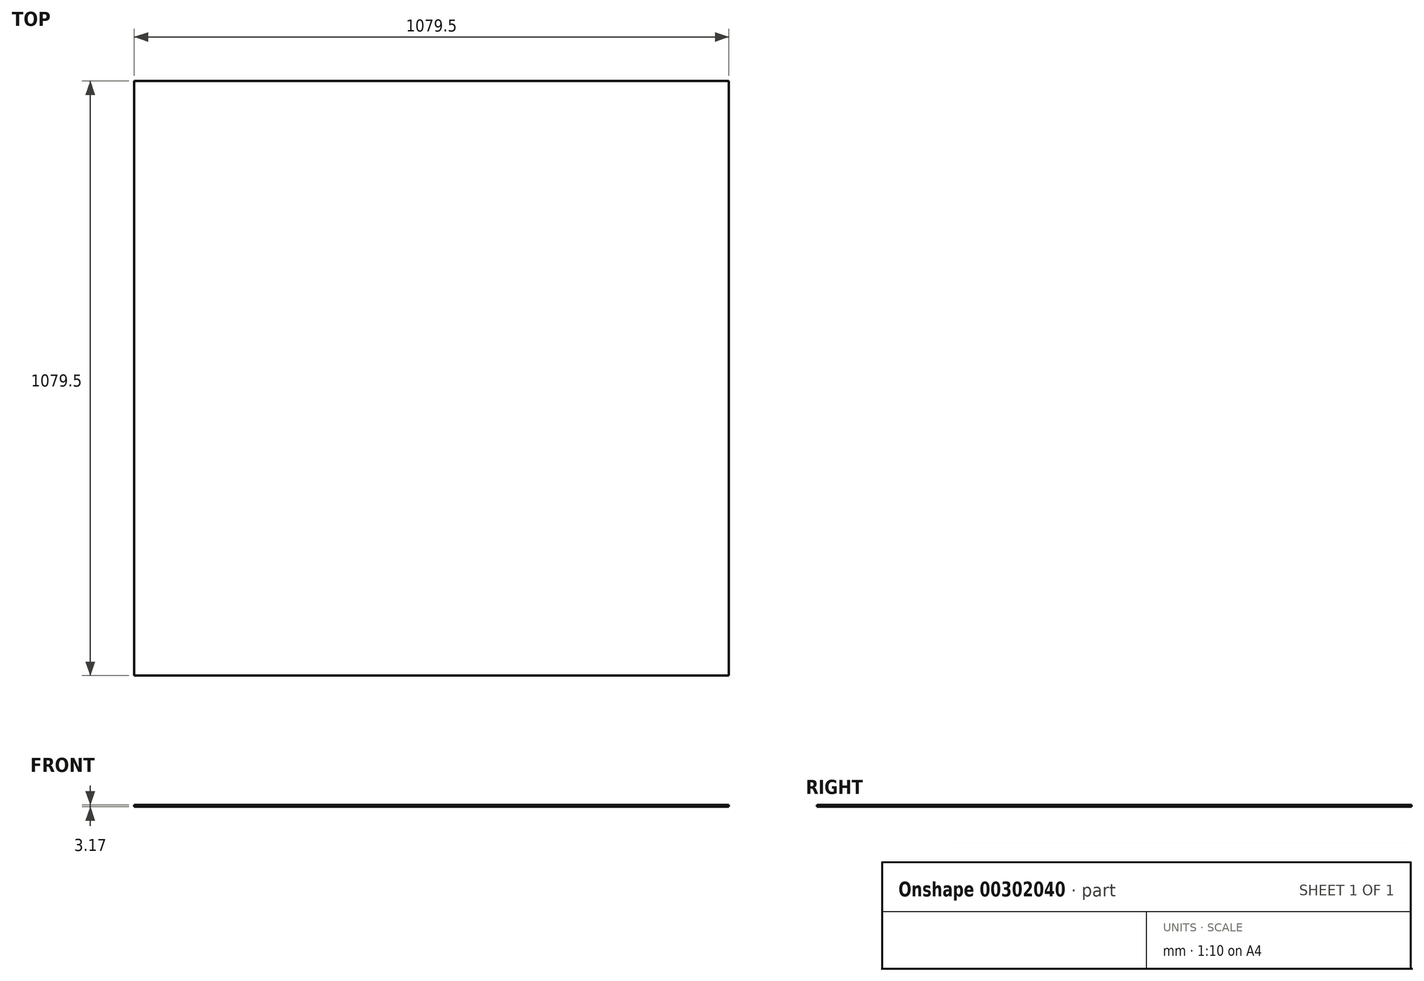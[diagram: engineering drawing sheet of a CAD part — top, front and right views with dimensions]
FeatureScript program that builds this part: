
annotation { "Feature Type Name" : "Feature", "Feature Type Description" : "" }
export const myFeature = defineFeature(function(context is Context, id is Id, definition is map)
    precondition{}
    {
        {
            var Q0;
            Q0=qCreatedBy(makeId("Top.planeOp"),FACE);
            var sketch = newSketch(context, id + "F0", { "sketchPlane" : qUnion([Q0])});
            skLineSegment(sketch, "E0.bottom", {"start": v(539.75, 539.75) * mm, "end": v(-539.75, 539.75) * mm});
            skLineSegment(sketch, "E0.top", {"start": v(539.75, -539.75) * mm, "end": v(-539.75, -539.75) * mm});
            skLineSegment(sketch, "E0.left", {"start": v(539.75, 539.75) * mm, "end": v(539.75, -539.75) * mm});
            skLineSegment(sketch, "E0.right", {"start": v(-539.75, 539.75) * mm, "end": v(-539.75, -539.75) * mm});
            skPoint(sketch, "E0.middle", {"position": v(0, 0) * mm});
            skSolve(sketch);
        }
        {
            var Q0;
            Q0 = qSketchRegion(id + "F0", true);
            extrude(context, id + "F1", {"entities" : qUnion([Q0]), "depth" : 3.17 * mm});
        }
    });
